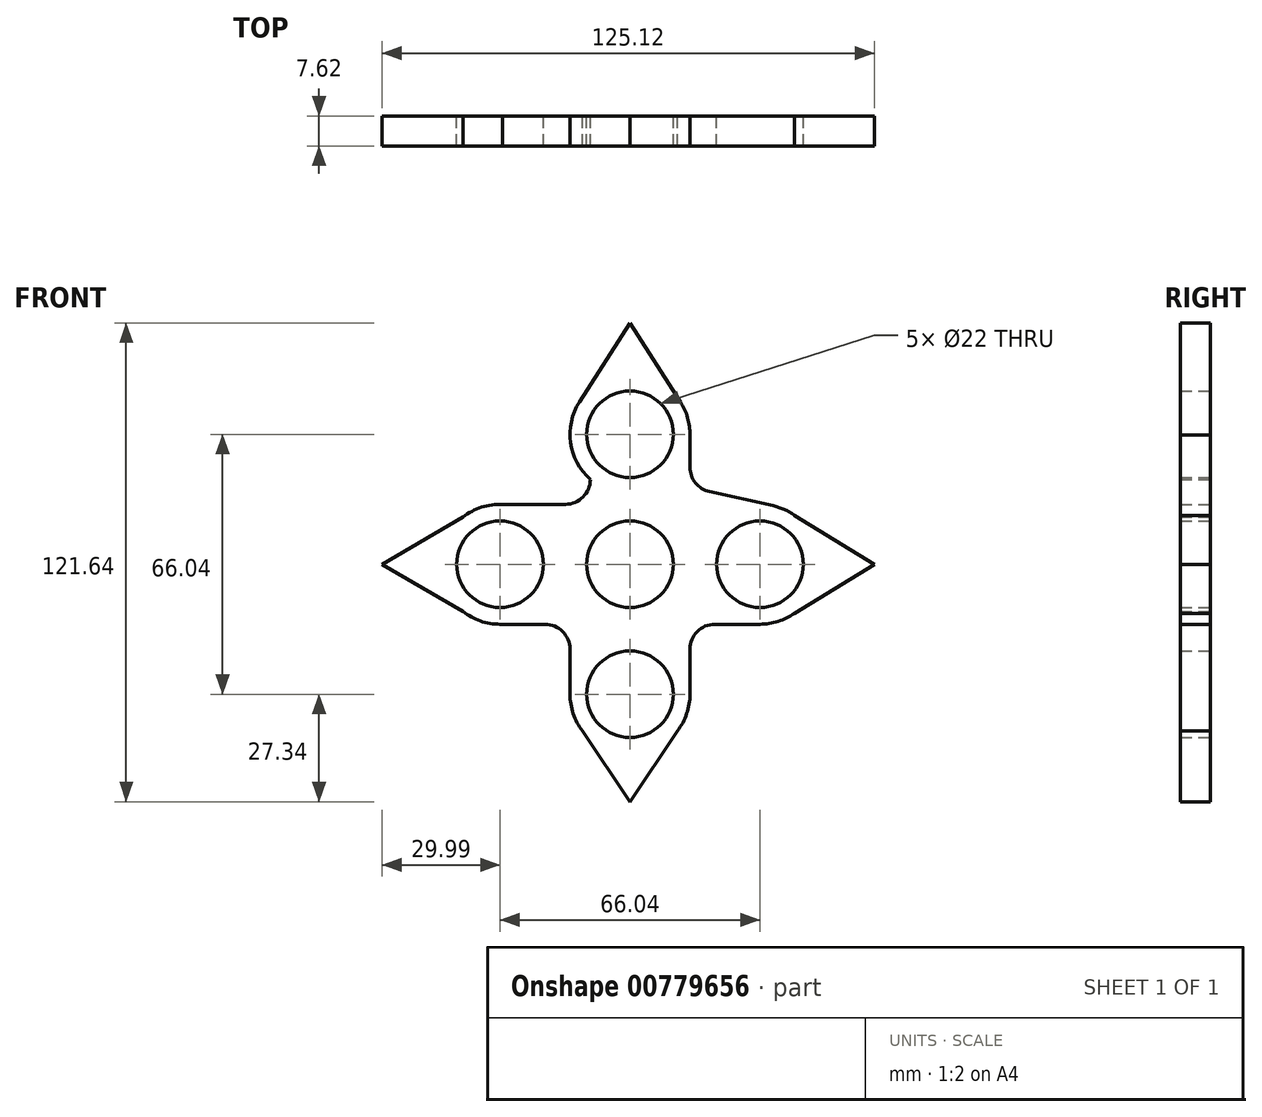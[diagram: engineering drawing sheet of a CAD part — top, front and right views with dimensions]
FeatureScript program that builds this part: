
annotation { "Feature Type Name" : "Feature", "Feature Type Description" : "" }
export const myFeature = defineFeature(function(context is Context, id is Id, definition is map)
    precondition{}
    {
        {
            var Q0;
            Q0=qCreatedBy(makeId("Front.planeOp"),FACE);
            var sketch = newSketch(context, id + "F0", { "sketchPlane" : qUnion([Q0])});
            skLineSegment(sketch, "E0", {"start": v(0, 0) * mm, "end": v(0, 33.02) * mm});
            skLineSegment(sketch, "E1", {"start": v(0, 33.02) * mm, "end": v(0, 0) * mm});
            skLineSegment(sketch, "E2", {"start": v(-33.02, 0) * mm, "end": v(0, 0) * mm});
            skLineSegment(sketch, "E3", {"start": v(0, 0) * mm, "end": v(33.02, 0) * mm});
            skLineSegment(sketch, "E4", {"start": v(0, 0) * mm, "end": v(0, -33.02) * mm});
            skCircle(sketch, "E5", {"center": v(0, 33.02) * mm, "radius": 15.24 * mm});
            skCircle(sketch, "E6", {"center": v(33.02, 0) * mm, "radius": 15.24 * mm});
            skCircle(sketch, "E7", {"center": v(0, -33.02) * mm, "radius": 15.24 * mm});
            skCircle(sketch, "E8", {"center": v(-33.02, 0) * mm, "radius": 15.24 * mm});
            skCircle(sketch, "E9", {"center": v(0, 0) * mm, "radius": 11 * mm});
            skLineSegment(sketch, "E10", {"start": v(15.24, 32.82) * mm, "end": v(15.24, 24.66) * mm});
            skLineSegment(sketch, "E11", {"start": v(-16.42, 15.23) * mm, "end": v(-33.65, 15.23) * mm});
            skLineSegment(sketch, "E12", {"start": v(-21.59, -15.24) * mm, "end": v(-33.02, -15.24) * mm});
            skArc(sketch, "E13.filletArc", {"start": v(-16.42, 15.23) * mm, "mid": v(-10.88, 18.46) * mm, "end": v(-10.98, 24.87) * mm});
            skLineSegment(sketch, "E14", {"start": v(-15.24, -21.6) * mm, "end": v(-15.24, -33.02) * mm});
            skArc(sketch, "E15.filletArc", {"start": v(-15.24, -21.6) * mm, "mid": v(-17.1, -17.1) * mm, "end": v(-21.59, -15.24) * mm});
            skLineSegment(sketch, "E16", {"start": v(20.21, 18.46) * mm, "end": v(36.33, 14.88) * mm});
            skLineSegment(sketch, "E17", {"start": v(21.59, -15.24) * mm, "end": v(33.02, -15.24) * mm});
            skPoint(sketch, "E18.newPointA", {"position": v(15.24, 0) * mm});
            skArc(sketch, "E18.filletArc", {"start": v(15.24, 24.66) * mm, "mid": v(16.64, 20.69) * mm, "end": v(20.21, 18.46) * mm});
            skPoint(sketch, "E19.newPointA", {"position": v(0, -15.24) * mm});
            skArc(sketch, "E19.filletArc", {"start": v(16.51, -15.24) * mm, "mid": v(15.87, -15.27) * mm, "end": v(15.24, -15.37) * mm});
            skLineSegment(sketch, "E20", {"start": v(-12.83, 41.24) * mm, "end": v(0, 61.28) * mm});
            skLineSegment(sketch, "E21", {"start": v(0, 61.28) * mm, "end": v(12.83, 41.24) * mm});
            skLineSegment(sketch, "E22", {"start": v(-42.43, 11.99) * mm, "end": v(-63, 0) * mm});
            skLineSegment(sketch, "E23", {"start": v(-63, 0) * mm, "end": v(-42.43, -11.99) * mm});
            skLineSegment(sketch, "E24", {"start": v(41.82, 12.44) * mm, "end": v(62.11, 0) * mm});
            skLineSegment(sketch, "E25", {"start": v(62.11, 0) * mm, "end": v(41.82, -12.44) * mm});
            skLineSegment(sketch, "E26", {"start": v(-13.24, -40.57) * mm, "end": v(0, -60.36) * mm});
            skLineSegment(sketch, "E27", {"start": v(0, -60.36) * mm, "end": v(13.24, -40.57) * mm});
            skCircle(sketch, "E28", {"center": v(33.02, 0) * mm, "radius": 11 * mm});
            skCircle(sketch, "E29", {"center": v(0, 33.02) * mm, "radius": 11 * mm});
            skCircle(sketch, "E30", {"center": v(-33.02, 0) * mm, "radius": 11 * mm});
            skCircle(sketch, "E31", {"center": v(0, -33.02) * mm, "radius": 11 * mm});
            skLineSegment(sketch, "E32", {"start": v(15.24, -21.6) * mm, "end": v(15.24, -33.02) * mm});
            skPoint(sketch, "E33.newPointB", {"position": v(16.51, -15.24) * mm});
            skArc(sketch, "E33.filletArc", {"start": v(21.59, -15.24) * mm, "mid": v(17.1, -17.1) * mm, "end": v(15.24, -21.6) * mm});
            skLineSegment(sketch, "E34", {"start": v(-10.98, 24.87) * mm, "end": v(-10.98, 33.02) * mm});
            skSolve(sketch);
        }
        {
            var Q0;
            Q0 = qSketchRegion(id + "F0", true);
            extrude(context, id + "F1", {"entities" : qUnion([Q0]), "depth" : 7.62 * mm, "offsetDistance" : 25.4 * mm});
        }
    });
